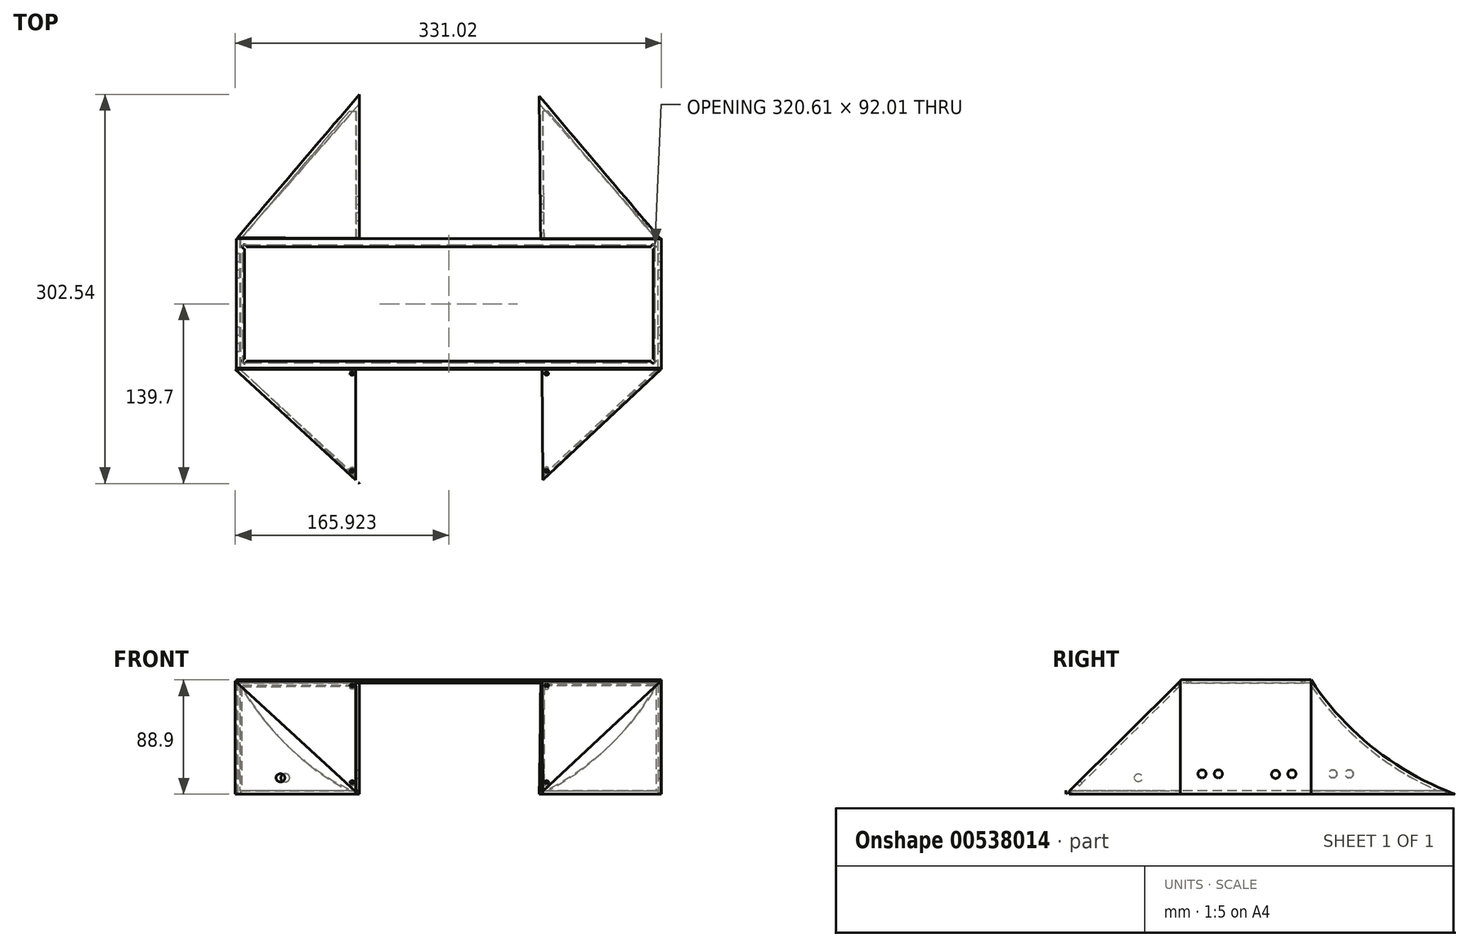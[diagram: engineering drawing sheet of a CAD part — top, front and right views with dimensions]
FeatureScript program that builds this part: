
annotation { "Feature Type Name" : "Feature", "Feature Type Description" : "" }
export const myFeature = defineFeature(function(context is Context, id is Id, definition is map)
    precondition{}
    {
        {
            var Q0;
            Q0=qCreatedBy(makeId("Right.planeOp"),FACE);
            var sketch = newSketch(context, id + "F0", { "sketchPlane" : qUnion([Q0])});
            skLineSegment(sketch, "E0", {"start": v(0, 0) * mm, "end": v(-88.9, 0) * mm});
            skLineSegment(sketch, "E1", {"start": v(-88.9, 0) * mm, "end": v(0, 88.9) * mm});
            skLineSegment(sketch, "E2", {"start": v(101.6, 0) * mm, "end": v(215.9, 0) * mm});
            skLineSegment(sketch, "E3", {"start": v(101.6, 0) * mm, "end": v(101.6, 88.9) * mm});
            skLineSegment(sketch, "E4", {"start": v(0, 88.9) * mm, "end": v(0, 0) * mm});
            skArc(sketch, "E5", {"start": v(101.6, 88.9) * mm, "mid": v(151.49, 35.11) * mm, "end": v(215.9, 0) * mm});
            skSolve(sketch);
        }
        {
            var Q0;
            Q0=qCreatedBy(makeId("Top.planeOp"),FACE);
            var sketch = newSketch(context, id + "F1", { "sketchPlane" : qUnion([Q0])});
            skLineSegment(sketch, "E6", {"start": v(-95.65, 101.6) * mm, "end": v(-95.65, 0) * mm});
            skLineSegment(sketch, "E7", {"start": v(234.55, 0) * mm, "end": v(234.55, 101.6) * mm});
            skLineSegment(sketch, "E8", {"start": v(-95.65, 0) * mm, "end": v(234.55, 0) * mm});
            skLineSegment(sketch, "E9", {"start": v(234.55, 101.6) * mm, "end": v(-95.65, 101.6) * mm});
            skSolve(sketch);
        }
        {
            var Q0;
            Q0=makeQuery(id+"F1.imprint","IMPRINT",FACE,{"disambiguationData":[TD([[makeQuery(id+"F1.imprint","IMPRINT",EDGE,{"derivedFrom":sQuery(id+"F1.wireOp",EDGE,"E6")}),1.0]])]});
            extrude(context, id + "F2", {"entities" : qUnion([Q0]), "depth" : 88.9 * mm, "offsetDistance" : 25.4 * mm});
        }
        {
            var Q0;
            Q0=makeQuery(id+"F2.opExtrude","SWEPT_FACE",FACE,{"disambiguationData":[OSD([sQuery(id+"F1.wireOp",EDGE,"E8")])]});
            var Q1;
            Q1=makeQuery(id+"F2.opExtrude","SWEPT_FACE",FACE,{"disambiguationData":[OSD([sQuery(id+"F1.wireOp",EDGE,"E9")])]});
            shell(context, id + "F3", {"entities" : qUnion([Q0, Q1]), "thickness" : 2.54 * mm});
        }
        {
            var Q0;
            Q0=qCreatedBy(makeId("Top.planeOp"),FACE);
            var sketch = newSketch(context, id + "F4", { "sketchPlane" : qUnion([Q0])});
            skLineSegment(sketch, "E10", {"start": v(0, 213.64) * mm, "end": v(-94.8, 102.22) * mm});
            skLineSegment(sketch, "E11", {"start": v(0, 213.64) * mm, "end": v(0, 101.72) * mm});
            skLineSegment(sketch, "E12", {"start": v(0, 101.72) * mm, "end": v(-94.8, 102.22) * mm});
            skLineSegment(sketch, "E13", {"start": v(139.7, 212.38) * mm, "end": v(233.9, 101.28) * mm});
            skLineSegment(sketch, "E14", {"start": v(233.9, 101.28) * mm, "end": v(140.82, 101.28) * mm});
            skLineSegment(sketch, "E15", {"start": v(140.82, 101.28) * mm, "end": v(139.7, 212.38) * mm});
            skLineSegment(sketch, "E16", {"start": v(0, -88.9) * mm, "end": v(-96.47, 0) * mm});
            skLineSegment(sketch, "E17", {"start": v(-96.47, 0) * mm, "end": v(0, 0) * mm});
            skLineSegment(sketch, "E18", {"start": v(0, 0) * mm, "end": v(0, -88.9) * mm});
            skLineSegment(sketch, "E19", {"start": v(234.3, 0) * mm, "end": v(139.7, -88.9) * mm});
            skLineSegment(sketch, "E20", {"start": v(139.7, -88.9) * mm, "end": v(138.93, 0) * mm});
            skLineSegment(sketch, "E21", {"start": v(138.93, 0) * mm, "end": v(234.3, 0) * mm});
            skSolve(sketch);
        }
        {
            var Q0;
            Q0=qSketchRegion(id+"F4",true);
            extrude(context, id + "F5", {"entities" : qUnion([Q0]), "depth" : 88.9 * mm, "offsetDistance" : 25.4 * mm});
        }
        {
            var Q0;
            Q0=qCreatedBy(makeId("Right.planeOp"),FACE);
            var sketch = newSketch(context, id + "F6", { "sketchPlane" : qUnion([Q0])});
            skArc(sketch, "E22", {"start": v(75.69, 141.85) * mm, "mid": v(128.62, 55.27) * mm, "end": v(213.71, 0) * mm});
            skLineSegment(sketch, "E23", {"start": v(75.69, 141.85) * mm, "end": v(232.54, 151.3) * mm});
            skLineSegment(sketch, "E24", {"start": v(232.54, 151.3) * mm, "end": v(213.71, 0) * mm});
            skLineSegment(sketch, "E25", {"start": v(55.29, 143) * mm, "end": v(-109.68, 111.35) * mm});
            skLineSegment(sketch, "E26", {"start": v(-109.68, 111.35) * mm, "end": v(-88.32, 0) * mm});
            skLineSegment(sketch, "E27", {"start": v(-88.32, 0) * mm, "end": v(55.29, 143) * mm});
            skSolve(sketch);
        }
        {
            var Q0;
            Q0=qSketchRegion(id+"F6",true);
            extrude(context, id + "F7", {"entities" : qUnion([Q0]), "operationType" : NewBodyOperationType.REMOVE, "oppositeDirection" : true, "depth" : 254 * mm, "offsetDistance" : 25.4 * mm});
        }
        {
            var Q0;
            Q0=qSketchRegion(id+"F6",true);
            extrude(context, id + "F8", {"entities" : qUnion([Q0]), "operationType" : NewBodyOperationType.REMOVE, "depth" : 381 * mm, "offsetDistance" : 25.4 * mm});
        }
        {
            var Q0;
            Q0=qCreatedBy(makeId("Top.planeOp"),FACE);
            var sketch = newSketch(context, id + "F9", { "sketchPlane" : qUnion([Q0])});
            skLineSegment(sketch, "E28.bottom", {"start": v(-89.3, 95.25) * mm, "end": v(228.2, 95.25) * mm});
            skLineSegment(sketch, "E28.top", {"start": v(-89.3, 6.35) * mm, "end": v(228.2, 6.35) * mm});
            skLineSegment(sketch, "E28.left", {"start": v(-89.3, 95.25) * mm, "end": v(-89.3, 6.35) * mm});
            skLineSegment(sketch, "E28.right", {"start": v(228.2, 95.25) * mm, "end": v(228.2, 6.35) * mm});
            skSolve(sketch);
        }
        {
            var Q0;
            Q0=qSketchRegion(id+"F9",true);
            var Q1;
            Q1=makeQuery(id+"F2.opExtrude","CAP_FACE",FACE,{"disambiguationData":[OSD([sQuery(id+"F1.wireOp",EDGE,"E6"),sQuery(id+"F1.wireOp",EDGE,"E7"),sQuery(id+"F1.wireOp",EDGE,"E8"),sQuery(id+"F1.wireOp",EDGE,"E9")])],"isStart":false});
            extrude(context, id + "F10", {"entities" : qUnion([Q0]), "operationType" : NewBodyOperationType.REMOVE, "depth" : 139.7 * mm, "endBoundEntityFace" : qUnion([Q1]), "hasOffset" : true, "offsetDistance" : 50.8 * mm, "offsetOppositeDirection" : true, "hasSecondDirection" : true, "secondDirectionOppositeDirection" : false, "secondDirectionDepth" : 47 * mm});
        }
        {
            var Q0;
            Q0=qCreatedBy(makeId("Right.planeOp"),FACE);
            var sketch = newSketch(context, id + "F11", { "sketchPlane" : qUnion([Q0])});
            skPoint(sketch, "E29", {"position": v(-32.35, 12.7) * mm});
            skCircle(sketch, "E30", {"center": v(-32.35, 12.7) * mm, "radius": 3.18 * mm});
            skSolve(sketch);
        }
        {
            var Q0;
            Q0=makeQuery(id+"F5.opExtrude","SWEPT_FACE",FACE,{"disambiguationData":[OSD([sQuery(id+"F4.wireOp",EDGE,"E12")])]});
            var Q1;
            Q1=makeQuery(id+"F5.opExtrude","SWEPT_FACE",FACE,{"disambiguationData":[OSD([sQuery(id+"F4.wireOp",EDGE,"E14")])]});
            var Q2;
            Q2=makeQuery(id+"F5.opExtrude","SWEPT_FACE",FACE,{"disambiguationData":[OSD([sQuery(id+"F4.wireOp",EDGE,"E17")])]});
            var Q3;
            Q3=makeQuery(id+"F5.opExtrude","SWEPT_FACE",FACE,{"disambiguationData":[OSD([sQuery(id+"F4.wireOp",EDGE,"E21")])]});
            shell(context, id + "F12", {"entities" : qUnion([Q0, Q1, Q2, Q3]), "thickness" : 2.54 * mm});
        }
        {
            var Q0;
            Q0=makeQuery(id+"F0.imprint","IMPRINT",FACE,{"disambiguationData":[TD([[makeQuery(id+"F0.imprint","IMPRINT",EDGE,{"derivedFrom":sQuery(id+"F0.wireOp",EDGE,"E0")}),-1.0]])]});
            var Q1;
            Q1=makeQuery(id+"F18.boolean.opBoolean","SPLIT",FACE,{"disambiguationData":[TD([makeQuery(id+"F5.opExtrude","SWEPT_FACE",FACE,{"disambiguationData":[OSD([sQuery(id+"F4.wireOp",EDGE,"E21")])]})])],"derivedFrom":makeQuery(id+"F5.opExtrude","SWEPT_FACE",FACE,{"disambiguationData":[OSD([sQuery(id+"F4.wireOp",EDGE,"E20")])]})});
            extrude(context, id + "F13", {"entities" : qUnion([Q0, Q1]), "operationType" : NewBodyOperationType.REMOVE, "oppositeDirection" : true, "depth" : 5.84 * mm, "offsetDistance" : 25.4 * mm, "symmetric" : true});
        }
        {
            var Q0;
            Q0=qSketchRegion(id+"F11",true);
            extrude(context, id + "F14", {"entities" : qUnion([Q0]), "operationType" : NewBodyOperationType.REMOVE, "oppositeDirection" : true, "depth" : 127 * mm, "offsetDistance" : 25.4 * mm});
        }
        {
            var Q0;
            Q0=qCreatedBy(makeId("Top.planeOp"),FACE);
            var sketch = newSketch(context, id + "F15", { "sketchPlane" : qUnion([Q0])});
            skLineSegment(sketch, "E31.bottom", {"start": v(-89.3, 76.2) * mm, "end": v(-54.3, 76.2) * mm});
            skLineSegment(sketch, "E31.top", {"start": v(-89.3, 25.4) * mm, "end": v(-54.3, 25.4) * mm});
            skLineSegment(sketch, "E31.left", {"start": v(-89.3, 76.2) * mm, "end": v(-89.3, 25.4) * mm});
            skLineSegment(sketch, "E31.right", {"start": v(-54.3, 76.2) * mm, "end": v(-54.3, 25.4) * mm});
            skLineSegment(sketch, "E32.bottom", {"start": v(193.2, 76.2) * mm, "end": v(228.2, 76.2) * mm});
            skLineSegment(sketch, "E32.top", {"start": v(193.2, 25.4) * mm, "end": v(228.2, 25.4) * mm});
            skLineSegment(sketch, "E32.left", {"start": v(193.2, 76.2) * mm, "end": v(193.2, 25.4) * mm});
            skLineSegment(sketch, "E32.right", {"start": v(228.2, 76.2) * mm, "end": v(228.2, 25.4) * mm});
            skSolve(sketch);
        }
        {
            var Q0;
            Q0=qSketchRegion(id+"F15",true);
            extrude(context, id + "F16", {"entities" : qUnion([Q0]), "operationType" : NewBodyOperationType.REMOVE, "depth" : 25.4 * mm, "offsetDistance" : 25.4 * mm});
        }
        {
            var Q0;
            Q0=qCreatedBy(makeId("Top.planeOp"),FACE);
            var sketch = newSketch(context, id + "F17", { "sketchPlane" : qUnion([Q0])});
            skLineSegment(sketch, "E33", {"start": v(-92.35, 0) * mm, "end": v(0, -87.18) * mm});
            skLineSegment(sketch, "E34", {"start": v(0, -87.18) * mm, "end": v(139.7, -87.18) * mm});
            skLineSegment(sketch, "E35", {"start": v(139.7, -87.18) * mm, "end": v(232.05, 0) * mm});
            skLineSegment(sketch, "E36", {"start": v(232.05, 0) * mm, "end": v(232.05, 101.6) * mm});
            skLineSegment(sketch, "E37", {"start": v(232.05, 101.6) * mm, "end": v(139.7, 206.42) * mm});
            skLineSegment(sketch, "E38", {"start": v(139.7, 206.42) * mm, "end": v(0, 206.42) * mm});
            skLineSegment(sketch, "E39", {"start": v(0, 206.42) * mm, "end": v(-92.35, 101.6) * mm});
            skLineSegment(sketch, "E40", {"start": v(-92.35, 101.6) * mm, "end": v(-92.35, 0) * mm});
            skSolve(sketch);
        }
        {
            var Q0;
            Q0=qSketchRegion(id+"F17",true);
            extrude(context, id + "F18", {"entities" : qUnion([Q0]), "operationType" : NewBodyOperationType.REMOVE, "depth" : 2.54 * mm, "offsetDistance" : 25.4 * mm});
        }
        {
            var Q0;
            Q0=qCreatedBy(makeId("Right.planeOp"),FACE);
            var sketch = newSketch(context, id + "F19", { "sketchPlane" : qUnion([Q0])});
            skCircle(sketch, "E41", {"center": v(86.87, 15.75) * mm, "radius": 3.18 * mm});
            skCircle(sketch, "E42", {"center": v(74.17, 15.39) * mm, "radius": 3.18 * mm});
            skCircle(sketch, "E43", {"center": v(17.02, 15.75) * mm, "radius": 3.18 * mm});
            skCircle(sketch, "E44", {"center": v(29.72, 15.75) * mm, "radius": 3.18 * mm});
            skCircle(sketch, "E45", {"center": v(118.67, 15.75) * mm, "radius": 3.18 * mm});
            skCircle(sketch, "E46", {"center": v(131.37, 15.75) * mm, "radius": 3.18 * mm});
            skSolve(sketch);
        }
        {
            var Q0;
            Q0=makeQuery(id+"F19.imprint","IMPRINT",FACE,{"disambiguationData":[TD([[makeQuery(id+"F19.imprint","IMPRINT",EDGE,{"derivedFrom":sQuery(id+"F19.wireOp",EDGE,"E41")}),1.0]])]});
            var Q1;
            Q1=makeQuery(id+"F19.imprint","IMPRINT",FACE,{"disambiguationData":[TD([[makeQuery(id+"F19.imprint","IMPRINT",EDGE,{"derivedFrom":sQuery(id+"F19.wireOp",EDGE,"E42")}),1.0]])]});
            var Q2;
            Q2=makeQuery(id+"F19.imprint","IMPRINT",FACE,{"disambiguationData":[TD([[makeQuery(id+"F19.imprint","IMPRINT",EDGE,{"derivedFrom":sQuery(id+"F19.wireOp",EDGE,"E43")}),1.0]])]});
            var Q3;
            Q3=makeQuery(id+"F19.imprint","IMPRINT",FACE,{"disambiguationData":[TD([[makeQuery(id+"F19.imprint","IMPRINT",EDGE,{"derivedFrom":sQuery(id+"F19.wireOp",EDGE,"E44")}),1.0]])]});
            extrude(context, id + "F20", {"entities" : qUnion([Q0, Q1, Q2, Q3]), "operationType" : NewBodyOperationType.REMOVE, "oppositeDirection" : true, "depth" : 762 * mm, "offsetDistance" : 25.4 * mm, "symmetric" : true});
        }
        {
            var Q0;
            Q0=makeQuery(id+"F19.imprint","IMPRINT",FACE,{"disambiguationData":[TD([[makeQuery(id+"F19.imprint","IMPRINT",EDGE,{"derivedFrom":sQuery(id+"F19.wireOp",EDGE,"E45")}),1.0]])]});
            var Q1;
            Q1=makeQuery(id+"F19.imprint","IMPRINT",FACE,{"disambiguationData":[TD([[makeQuery(id+"F19.imprint","IMPRINT",EDGE,{"derivedFrom":sQuery(id+"F19.wireOp",EDGE,"E46")}),1.0]])]});
            extrude(context, id + "F21", {"entities" : qUnion([Q0, Q1]), "operationType" : NewBodyOperationType.REMOVE, "depth" : 152.4 * mm, "offsetDistance" : 25.4 * mm});
        }
        {
            var Q0;
            Q0=makeQuery(id+"F19.imprint","IMPRINT",FACE,{"disambiguationData":[TD([[makeQuery(id+"F19.imprint","IMPRINT",EDGE,{"derivedFrom":sQuery(id+"F19.wireOp",EDGE,"E45")}),1.0]])]});
            var Q1;
            Q1=makeQuery(id+"F19.imprint","IMPRINT",FACE,{"disambiguationData":[TD([[makeQuery(id+"F19.imprint","IMPRINT",EDGE,{"derivedFrom":sQuery(id+"F19.wireOp",EDGE,"E46")}),1.0]])]});
            extrude(context, id + "F22", {"entities" : qUnion([Q0, Q1]), "operationType" : NewBodyOperationType.REMOVE, "oppositeDirection" : true, "depth" : 25.4 * mm, "offsetDistance" : 25.4 * mm});
        }
        {
            var Q0;
            Q0=makeQuery(id+"F2.opExtrude","CAP_FACE",FACE,{"disambiguationData":[OSD([sQuery(id+"F1.wireOp",EDGE,"E6"),sQuery(id+"F1.wireOp",EDGE,"E7"),sQuery(id+"F1.wireOp",EDGE,"E8"),sQuery(id+"F1.wireOp",EDGE,"E9")])],"isStart":false});
            var sketch = newSketch(context, id + "F23", { "sketchPlane" : qUnion([Q0])});
            skPoint(sketch, "E47", {"position": v(-89.3, 95.25) * mm});
            skPoint(sketch, "E48", {"position": v(-89.3, 6.35) * mm});
            skPoint(sketch, "E49", {"position": v(228.2, 6.35) * mm});
            skPoint(sketch, "E50", {"position": v(228.2, 95.25) * mm});
            skSolve(sketch);
        }
        {
            var Q0;
            Q0=sQuery(id+"F23.wireOp",VERTEX,"E47");
            var Q1;
            Q1=sQuery(id+"F23.wireOp",VERTEX,"E48");
            var Q2;
            Q2=sQuery(id+"F23.wireOp",VERTEX,"E49");
            var Q3;
            Q3=sQuery(id+"F23.wireOp",VERTEX,"E50");
            var Q4;
            Q4=makeQuery(id+"F2.opExtrude","SWEPT_BODY",BODY,{"disambiguationData":[OSD([sQuery(id+"F1.wireOp",EDGE,"E6"),sQuery(id+"F1.wireOp",EDGE,"E7"),sQuery(id+"F1.wireOp",EDGE,"E8"),sQuery(id+"F1.wireOp",EDGE,"E9")])]});
            var Q5;
            Q5=makeQuery(id+"F5.opExtrude","SWEPT_BODY",BODY,{"disambiguationData":[OSD([sQuery(id+"F4.wireOp",EDGE,"E10"),sQuery(id+"F4.wireOp",EDGE,"E11"),sQuery(id+"F4.wireOp",EDGE,"E12")])]});
            var Q6;
            Q6=makeQuery(id+"F5.opExtrude","SWEPT_BODY",BODY,{"disambiguationData":[OSD([sQuery(id+"F4.wireOp",EDGE,"E13"),sQuery(id+"F4.wireOp",EDGE,"E14"),sQuery(id+"F4.wireOp",EDGE,"E15")])]});
            var Q7;
            Q7=makeQuery(id+"F7.boolean.opBoolean","SPLIT",BODY,{"disambiguationData":[OD(0.0)],"derivedFrom":makeQuery(id+"F5.opExtrude","SWEPT_BODY",BODY,{"disambiguationData":[OSD([sQuery(id+"F4.wireOp",EDGE,"E16"),sQuery(id+"F4.wireOp",EDGE,"E17"),sQuery(id+"F4.wireOp",EDGE,"E18")])]})});
            var Q8;
            Q8=makeQuery(id+"F7.boolean.opBoolean","SPLIT",BODY,{"disambiguationData":[OD(1.0)],"derivedFrom":makeQuery(id+"F5.opExtrude","SWEPT_BODY",BODY,{"disambiguationData":[OSD([sQuery(id+"F4.wireOp",EDGE,"E16"),sQuery(id+"F4.wireOp",EDGE,"E17"),sQuery(id+"F4.wireOp",EDGE,"E18")])]})});
            var Q9;
            Q9=makeQuery(id+"F8.boolean.opBoolean","SPLIT",BODY,{"disambiguationData":[OD(1.0)],"derivedFrom":makeQuery(id+"F5.opExtrude","SWEPT_BODY",BODY,{"disambiguationData":[OSD([sQuery(id+"F4.wireOp",EDGE,"E19"),sQuery(id+"F4.wireOp",EDGE,"E20"),sQuery(id+"F4.wireOp",EDGE,"E21")])]})});
            hole(context, id + "F24", {"style" : HoleStyle.SIMPLE, "endStyle" : HoleEndStyle.BLIND, "holeDiameter" : 3.17 * mm, "holeDepth" : 254 * mm, "isTappedThrough" : true, "tappedDepth" : 12.7 * mm, "tapClearance" : 3, "locations" : qUnion([Q0, Q1, Q2, Q3]), "scope" : qUnion([Q4, Q5, Q6, Q7, Q8, Q9])});
        }
        {
            var Q0;
            {var subQ0=sQuery(id+"F4.wireOp",EDGE,"E16");Q0=makeQuery(id+"F7.boolean.opBoolean","COPY",FACE,{"disambiguationData":[TD([makeQuery(id+"F5.opExtrude","SWEPT_FACE",FACE,{"disambiguationData":[OSD([subQ0])]})])],"derivedFrom":makeQuery(id+"F7.opExtrude","SWEPT_FACE",FACE,{"disambiguationData":[OSD([sQuery(id+"F6.wireOp",EDGE,"E27")])]})});}
            var sketch = newSketch(context, id + "F25", { "sketchPlane" : qUnion([Q0])});
            skPoint(sketch, "E51", {"position": v(-5.69, 57.17) * mm});
            skPoint(sketch, "E52", {"position": v(145.42, 57.17) * mm});
            skPoint(sketch, "E53", {"position": v(-5.69, -49.41) * mm});
            skPoint(sketch, "E54", {"position": v(145.42, -49.41) * mm});
            skSolve(sketch);
        }
        {
            var Q0;
            Q0=sQuery(id+"F25.wireOp",VERTEX,"E51");
            var Q1;
            Q1=sQuery(id+"F25.wireOp",VERTEX,"E53");
            var Q2;
            Q2=sQuery(id+"F25.wireOp",VERTEX,"E52");
            var Q3;
            Q3=sQuery(id+"F25.wireOp",VERTEX,"E54");
            var Q4;
            Q4=makeQuery(id+"F7.boolean.opBoolean","SPLIT",BODY,{"disambiguationData":[OD(1.0)],"derivedFrom":makeQuery(id+"F5.opExtrude","SWEPT_BODY",BODY,{"disambiguationData":[OSD([sQuery(id+"F4.wireOp",EDGE,"E16"),sQuery(id+"F4.wireOp",EDGE,"E17"),sQuery(id+"F4.wireOp",EDGE,"E18")])]})});
            var Q5;
            Q5=makeQuery(id+"F8.boolean.opBoolean","SPLIT",BODY,{"disambiguationData":[OD(1.0)],"derivedFrom":makeQuery(id+"F5.opExtrude","SWEPT_BODY",BODY,{"disambiguationData":[OSD([sQuery(id+"F4.wireOp",EDGE,"E19"),sQuery(id+"F4.wireOp",EDGE,"E20"),sQuery(id+"F4.wireOp",EDGE,"E21")])]})});
            hole(context, id + "F26", {"style" : HoleStyle.SIMPLE, "endStyle" : HoleEndStyle.BLIND, "holeDiameter" : 3.17 * mm, "holeDepth" : 254 * mm, "isTappedThrough" : true, "tappedDepth" : 12.7 * mm, "tapClearance" : 3, "locations" : qUnion([Q0, Q1, Q2, Q3]), "scope" : qUnion([Q4, Q5])});
        }
    });
